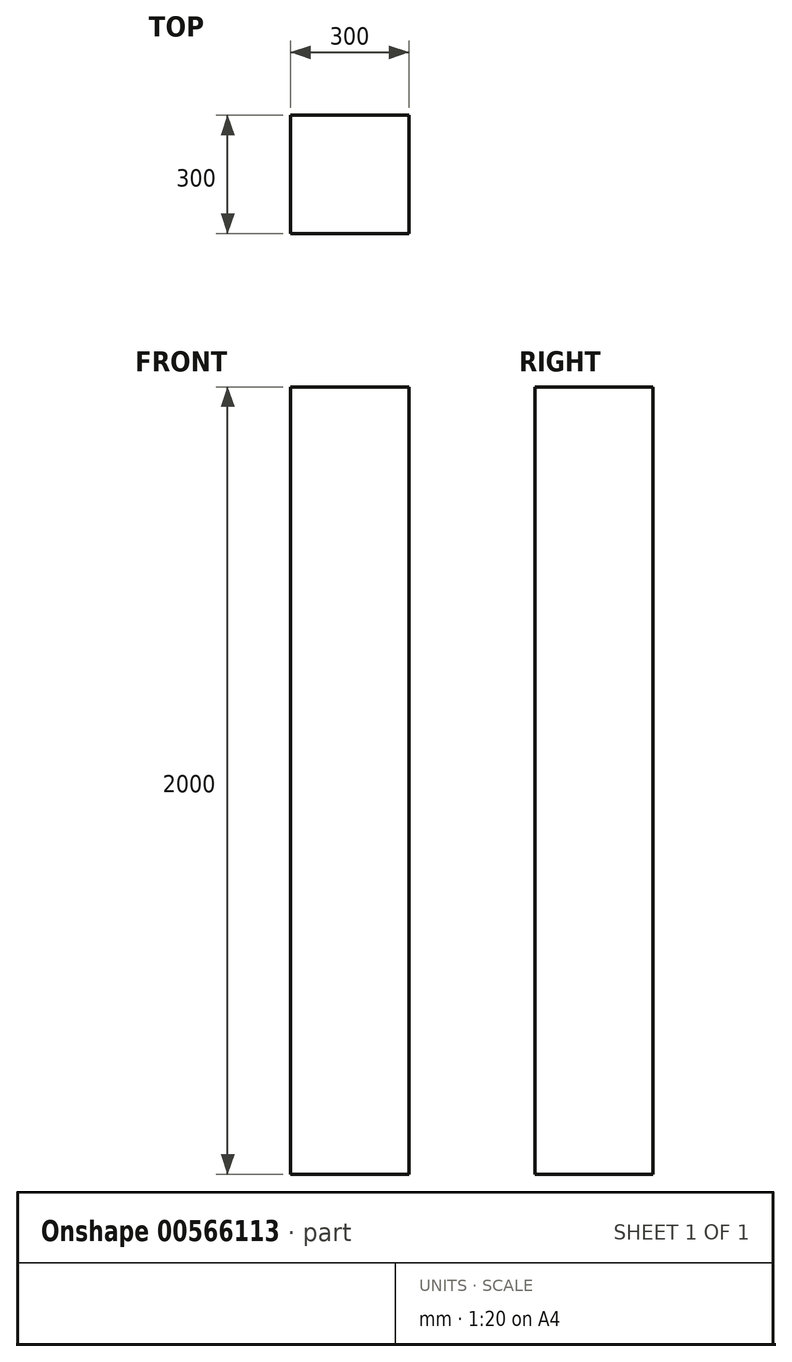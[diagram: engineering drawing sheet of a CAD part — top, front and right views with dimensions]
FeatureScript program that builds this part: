
annotation { "Feature Type Name" : "Feature", "Feature Type Description" : "" }
export const myFeature = defineFeature(function(context is Context, id is Id, definition is map)
    precondition{}
    {
        {
            var Q0;
            Q0=qCreatedBy(makeId("Top.planeOp"),FACE);
            var sketch = newSketch(context, id + "F0", { "sketchPlane" : qUnion([Q0])});
            skLineSegment(sketch, "E0.bottom", {"start": v(150, 150) * mm, "end": v(-150, 150) * mm});
            skLineSegment(sketch, "E0.top", {"start": v(150, -150) * mm, "end": v(-150, -150) * mm});
            skLineSegment(sketch, "E0.left", {"start": v(150, 150) * mm, "end": v(150, -150) * mm});
            skLineSegment(sketch, "E0.right", {"start": v(-150, 150) * mm, "end": v(-150, -150) * mm});
            skPoint(sketch, "E0.middle", {"position": v(0, 0) * mm});
            skSolve(sketch);
        }
        {
            var Q0;
            Q0 = qSketchRegion(id + "F0", true);
            extrude(context, id + "F1", {"entities" : qUnion([Q0]), "depth" : 2000 * mm, "offsetDistance" : 25 * mm});
        }
    });
